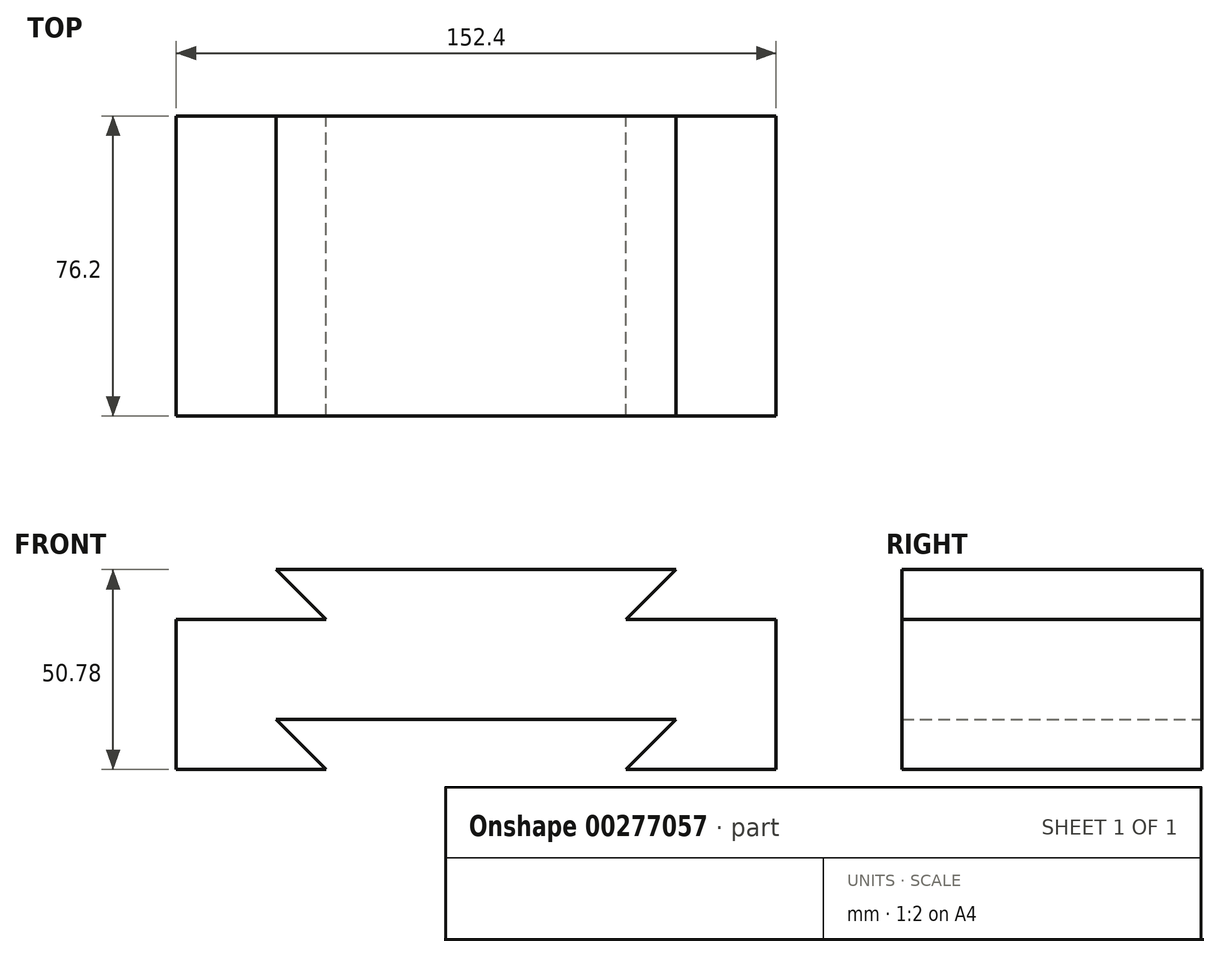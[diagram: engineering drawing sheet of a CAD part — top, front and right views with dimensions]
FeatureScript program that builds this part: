
annotation { "Feature Type Name" : "Feature", "Feature Type Description" : "" }
export const myFeature = defineFeature(function(context is Context, id is Id, definition is map)
    precondition{}
    {
        {
            var Q0;
            Q0=qCreatedBy(makeId("Right.planeOp"),FACE);
            var sketch = newSketch(context, id + "F0", { "sketchPlane" : qUnion([Q0])});
            skLineSegment(sketch, "E0.bottom", {"start": v(-38.1, 25.4) * mm, "end": v(38.1, 25.4) * mm});
            skLineSegment(sketch, "E0.top", {"start": v(-38.1, -25.4) * mm, "end": v(38.1, -25.4) * mm});
            skLineSegment(sketch, "E0.left", {"start": v(-38.1, 25.4) * mm, "end": v(-38.1, -25.4) * mm});
            skLineSegment(sketch, "E0.right", {"start": v(38.1, 25.4) * mm, "end": v(38.1, -25.4) * mm});
            skPoint(sketch, "E0.middle", {"position": v(0, 0) * mm});
            skSolve(sketch);
        }
        {
            var Q0;
            Q0=makeQuery(id+"F0.imprint","IMPRINT",FACE,{"disambiguationData":[TD([[makeQuery(id+"F0.imprint","IMPRINT",EDGE,{"derivedFrom":sQuery(id+"F0.wireOp",EDGE,"E0.bottom")}),-1.0]])]});
            extrude(context, id + "F1", {"entities" : qUnion([Q0]), "depth" : 76.2 * mm});
        }
        {
            var Q0;
            Q0=makeQuery(id+"F1.opExtrude","CAP_FACE",FACE,{"disambiguationData":[OSD([sQuery(id+"F0.wireOp",EDGE,"E0.bottom"),sQuery(id+"F0.wireOp",EDGE,"E0.top"),sQuery(id+"F0.wireOp",EDGE,"E0.left"),sQuery(id+"F0.wireOp",EDGE,"E0.right")])],"isStart":true});
            extrude(context, id + "F2", {"entities" : qUnion([Q0]), "operationType" : NewBodyOperationType.ADD, "depth" : 76.2 * mm});
        }
        {
            var Q0;
            {var subQ0=sQuery(id+"F0.wireOp",EDGE,"E0.right");Q0=makeQuery(id+"F2.boolean.opBoolean","MERGE",FACE,{"derivedFrom":[makeQuery(id+"F1.opExtrude","SWEPT_FACE",FACE,{"disambiguationData":[OSD([subQ0])]}),makeQuery(id+"F2.opExtrude","SWEPT_FACE",FACE,{"disambiguationData":[OSD([subQ0])]})]});}
            var sketch = newSketch(context, id + "F3", { "sketchPlane" : qUnion([Q0])});
            skLineSegment(sketch, "E1", {"start": v(-76.2, -25.4) * mm, "end": v(-38.1, -25.4) * mm});
            skLineSegment(sketch, "E2", {"start": v(-38.1, -25.4) * mm, "end": v(-50.8, -25.4) * mm});
            skLineSegment(sketch, "E3", {"start": v(-50.8, -25.4) * mm, "end": v(-50.8, -12.7) * mm});
            skLineSegment(sketch, "E4", {"start": v(-50.8, -12.7) * mm, "end": v(-38.1, -25.4) * mm});
            skLineSegment(sketch, "E5", {"start": v(76.2, -25.4) * mm, "end": v(38.09, -25.4) * mm});
            skLineSegment(sketch, "E6", {"start": v(38.09, -25.4) * mm, "end": v(50.79, -25.4) * mm});
            skLineSegment(sketch, "E7", {"start": v(50.79, -25.4) * mm, "end": v(50.79, -12.7) * mm});
            skLineSegment(sketch, "E8", {"start": v(50.79, -12.7) * mm, "end": v(38.09, -25.4) * mm});
            skLineSegment(sketch, "E9", {"start": v(-76.2, 25.4) * mm, "end": v(-76.2, 12.69) * mm});
            skLineSegment(sketch, "E10", {"start": v(-76.2, 12.69) * mm, "end": v(-50.81, 12.69) * mm});
            skLineSegment(sketch, "E11", {"start": v(-50.81, 12.69) * mm, "end": v(-50.81, 25.4) * mm});
            skLineSegment(sketch, "E12", {"start": v(-50.81, 12.69) * mm, "end": v(-38.12, 12.69) * mm});
            skLineSegment(sketch, "E13", {"start": v(-38.12, 12.69) * mm, "end": v(-50.81, 25.4) * mm});
            skLineSegment(sketch, "E14", {"start": v(76.2, 25.4) * mm, "end": v(76.2, 12.69) * mm});
            skLineSegment(sketch, "E15", {"start": v(76.2, 12.69) * mm, "end": v(50.81, 12.69) * mm});
            skLineSegment(sketch, "E16", {"start": v(50.81, 12.69) * mm, "end": v(38.1, 12.69) * mm});
            skLineSegment(sketch, "E17", {"start": v(38.1, 12.69) * mm, "end": v(50.81, 25.4) * mm});
            skLineSegment(sketch, "E18", {"start": v(50.79, -12.7) * mm, "end": v(-50.8, -12.7) * mm});
            skSolve(sketch);
        }
        {
            var Q0;
            {var subQ0=sQuery(id+"F3.wireOp",EDGE,"E4");Q0=makeQuery(id+"F3.imprint","IMPRINT",FACE,{"disambiguationData":[TD([[makeQuery(id+"F3.imprint","IMPRINT",EDGE,{"derivedFrom":subQ0}),1.0]])]});}
            var Q1;
            {var subQ1=sQuery(id+"F3.wireOp",EDGE,"E14");Q1=makeQuery(id+"F3.imprint","IMPRINT",FACE,{"disambiguationData":[TD([[makeQuery(id+"F3.imprint","IMPRINT",EDGE,{"derivedFrom":subQ1}),-1.0]])]});}
            var Q2;
            Q2=makeQuery(id+"F3.imprint","IMPRINT",FACE,{"disambiguationData":[TD([[makeQuery(id+"F3.imprint","IMPRINT",EDGE,{"derivedFrom":sQuery(id+"F3.wireOp",EDGE,"E11")}),-1.0]])]});
            var Q3;
            {var subQ0=sQuery(id+"F3.wireOp",EDGE,"E9");Q3=makeQuery(id+"F3.imprint","IMPRINT",FACE,{"disambiguationData":[TD([[makeQuery(id+"F3.imprint","IMPRINT",EDGE,{"derivedFrom":subQ0}),1.0]])]});}
            extrude(context, id + "F4", {"entities" : qUnion([Q0, Q1, Q2, Q3]), "operationType" : NewBodyOperationType.REMOVE, "oppositeDirection" : true, "depth" : 169.16 * mm});
        }
    });
